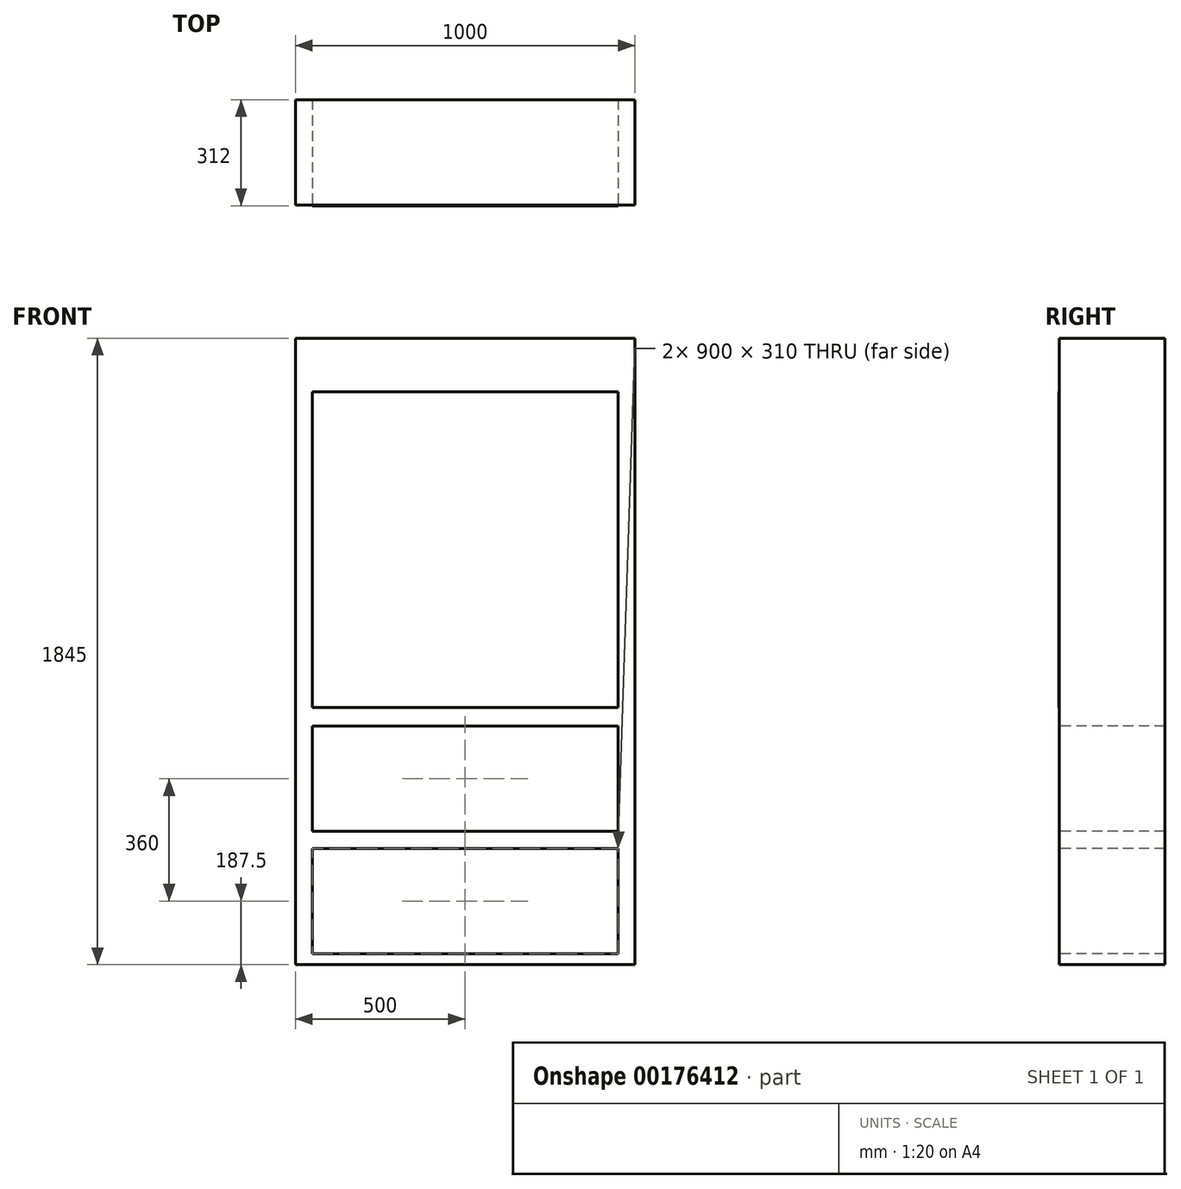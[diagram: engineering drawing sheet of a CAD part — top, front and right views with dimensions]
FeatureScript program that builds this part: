
annotation { "Feature Type Name" : "Feature", "Feature Type Description" : "" }
export const myFeature = defineFeature(function(context is Context, id is Id, definition is map)
    precondition{}
    {
        {
            var Q0;
            Q0=qCreatedBy(makeId("Front.planeOp"),FACE);
            var sketch = newSketch(context, id + "F0", { "sketchPlane" : qUnion([Q0])});
            skLineSegment(sketch, "E0.bottom", {"start": v(500, 922.5) * mm, "end": v(-500, 922.5) * mm});
            skLineSegment(sketch, "E0.top", {"start": v(500, -922.5) * mm, "end": v(-500, -922.5) * mm});
            skLineSegment(sketch, "E0.left", {"start": v(500, 922.5) * mm, "end": v(500, -922.5) * mm});
            skLineSegment(sketch, "E0.right", {"start": v(-500, 922.5) * mm, "end": v(-500, -922.5) * mm});
            skPoint(sketch, "E0.middle", {"position": v(0, 0) * mm});
            skSolve(sketch);
        }
        {
            var Q0;
            Q0 = qSketchRegion(id + "F0", true);
            extrude(context, id + "F1", {"entities" : qUnion([Q0]), "depth" : 310 * mm});
        }
        {
            var Q0;
            Q0=makeQuery(id+"F1.opExtrude","CAP_FACE",FACE,{"disambiguationData":[OSD([sQuery(id+"F0.wireOp",EDGE,"E0.bottom"),sQuery(id+"F0.wireOp",EDGE,"E0.top"),sQuery(id+"F0.wireOp",EDGE,"E0.left"),sQuery(id+"F0.wireOp",EDGE,"E0.right")])],"isStart":false});
            var sketch = newSketch(context, id + "F4", { "sketchPlane" : qUnion([Q0])});
            skLineSegment(sketch, "E1.bottom", {"start": v(450, 765) * mm, "end": v(-450, 765) * mm});
            skLineSegment(sketch, "E1.top", {"start": v(450, -165) * mm, "end": v(-450, -165) * mm});
            skLineSegment(sketch, "E1.left", {"start": v(450, 765) * mm, "end": v(450, -165) * mm});
            skLineSegment(sketch, "E1.right", {"start": v(-450, 765) * mm, "end": v(-450, -165) * mm});
            skPoint(sketch, "E1.middle", {"position": v(0, 300) * mm});
            skSolve(sketch);
        }
        {
            var Q0;
            Q0=makeQuery(id+"F4.imprint","IMPRINT",FACE,{"disambiguationData":[TD([[makeQuery(id+"F4.imprint","IMPRINT",EDGE,{"derivedFrom":sQuery(id+"F4.wireOp",EDGE,"E1.bottom")}),1.0]])]});
            extrude(context, id + "F2", {"entities" : qUnion([Q0]), "depth" : 2 * mm});
        }
        {
            var Q0;
            Q0=makeQuery(id+"F1.opExtrude","CAP_FACE",FACE,{"disambiguationData":[OSD([sQuery(id+"F0.wireOp",EDGE,"E0.bottom"),sQuery(id+"F0.wireOp",EDGE,"E0.top"),sQuery(id+"F0.wireOp",EDGE,"E0.left"),sQuery(id+"F0.wireOp",EDGE,"E0.right")])],"isStart":false});
            var sketch = newSketch(context, id + "F5", { "sketchPlane" : qUnion([Q0])});
            skLineSegment(sketch, "E2.bottom", {"start": v(450, -220) * mm, "end": v(-450, -220) * mm});
            skLineSegment(sketch, "E2.top", {"start": v(450, -530) * mm, "end": v(-450, -530) * mm});
            skLineSegment(sketch, "E2.left", {"start": v(450, -220) * mm, "end": v(450, -530) * mm});
            skLineSegment(sketch, "E2.right", {"start": v(-450, -220) * mm, "end": v(-450, -530) * mm});
            skPoint(sketch, "E2.middle", {"position": v(0, -375) * mm});
            skPoint(sketch, "E3.0", {"position": v(0, 0) * mm});
            skLineSegment(sketch, "E4.bottom", {"start": v(450, -890) * mm, "end": v(-450, -890) * mm});
            skLineSegment(sketch, "E4.top", {"start": v(450, -580) * mm, "end": v(-450, -580) * mm});
            skLineSegment(sketch, "E4.left", {"start": v(450, -890) * mm, "end": v(450, -580) * mm});
            skLineSegment(sketch, "E4.right", {"start": v(-450, -890) * mm, "end": v(-450, -580) * mm});
            skPoint(sketch, "E4.middle", {"position": v(0, -735) * mm});
            skSolve(sketch);
        }
        {
            var Q0;
            Q0=makeQuery(id+"F5.imprint","IMPRINT",FACE,{"disambiguationData":[TD([[makeQuery(id+"F5.imprint","IMPRINT",EDGE,{"derivedFrom":sQuery(id+"F5.wireOp",EDGE,"E2.bottom")}),1.0]])]});
            var Q1;
            Q1=makeQuery(id+"F5.imprint","IMPRINT",FACE,{"disambiguationData":[TD([[makeQuery(id+"F5.imprint","IMPRINT",EDGE,{"derivedFrom":sQuery(id+"F5.wireOp",EDGE,"E4.bottom")}),-1.0]])]});
            extrude(context, id + "F3", {"entities" : qUnion([Q0, Q1]), "operationType" : NewBodyOperationType.REMOVE, "endBound" : BoundingType.THROUGH_ALL, "oppositeDirection" : true, "depth" : 25 * mm});
        }
    });
